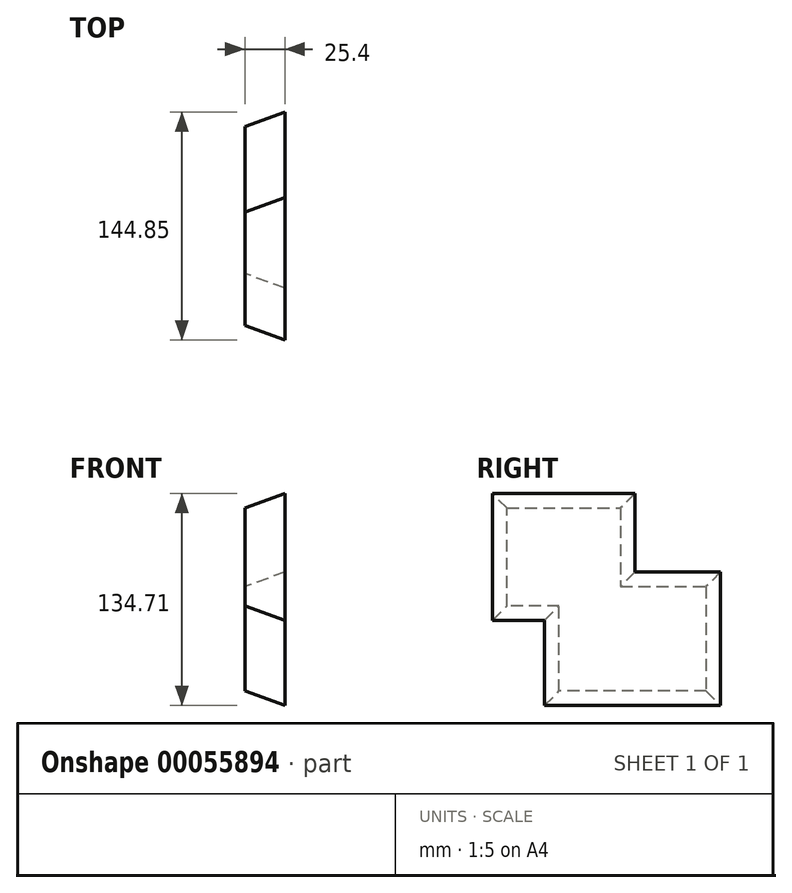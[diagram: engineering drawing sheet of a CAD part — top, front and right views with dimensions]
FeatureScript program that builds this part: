
annotation { "Feature Type Name" : "Feature", "Feature Type Description" : "" }
export const myFeature = defineFeature(function(context is Context, id is Id, definition is map)
    precondition{}
    {
        {
            var Q0;
            Q0=qCreatedBy(makeId("Right.planeOp"),FACE);
            var sketch = newSketch(context, id + "F0", { "sketchPlane" : qUnion([Q0])});
            skLineSegment(sketch, "E0.bottom", {"start": v(-62.34, 53.55) * mm, "end": v(9.68, 53.55) * mm});
            skLineSegment(sketch, "E0.top", {"start": v(-62.34, -8.6) * mm, "end": v(-29.32, -8.6) * mm});
            skLineSegment(sketch, "E0.left", {"start": v(-62.34, 53.55) * mm, "end": v(-62.34, -8.6) * mm});
            skLineSegment(sketch, "E0.right", {"start": v(9.68, 53.55) * mm, "end": v(9.68, 3.63) * mm});
            skLineSegment(sketch, "E1.bottom", {"start": v(9.68, 3.63) * mm, "end": v(64.01, 3.63) * mm});
            skLineSegment(sketch, "E1.top", {"start": v(-29.32, -62.67) * mm, "end": v(64.01, -62.67) * mm});
            skLineSegment(sketch, "E1.left", {"start": v(-29.32, -8.6) * mm, "end": v(-29.32, -62.67) * mm});
            skLineSegment(sketch, "E1.right", {"start": v(64.01, 3.63) * mm, "end": v(64.01, -62.67) * mm});
            skSolve(sketch);
        }
        {
            var Q0;
            Q0=makeQuery(id+"F0.imprint","IMPRINT",FACE,{"disambiguationData":[TD([[makeQuery(id+"F0.imprint","IMPRINT",EDGE,{"derivedFrom":sQuery(id+"F0.wireOp",EDGE,"E0.bottom")}),-1.0]])]});
            extrude(context, id + "F1", {"entities" : qUnion([Q0]), "depth" : 25.4 * mm, "hasDraft" : true, "draftAngle" : 20 * degree});
        }
    });
